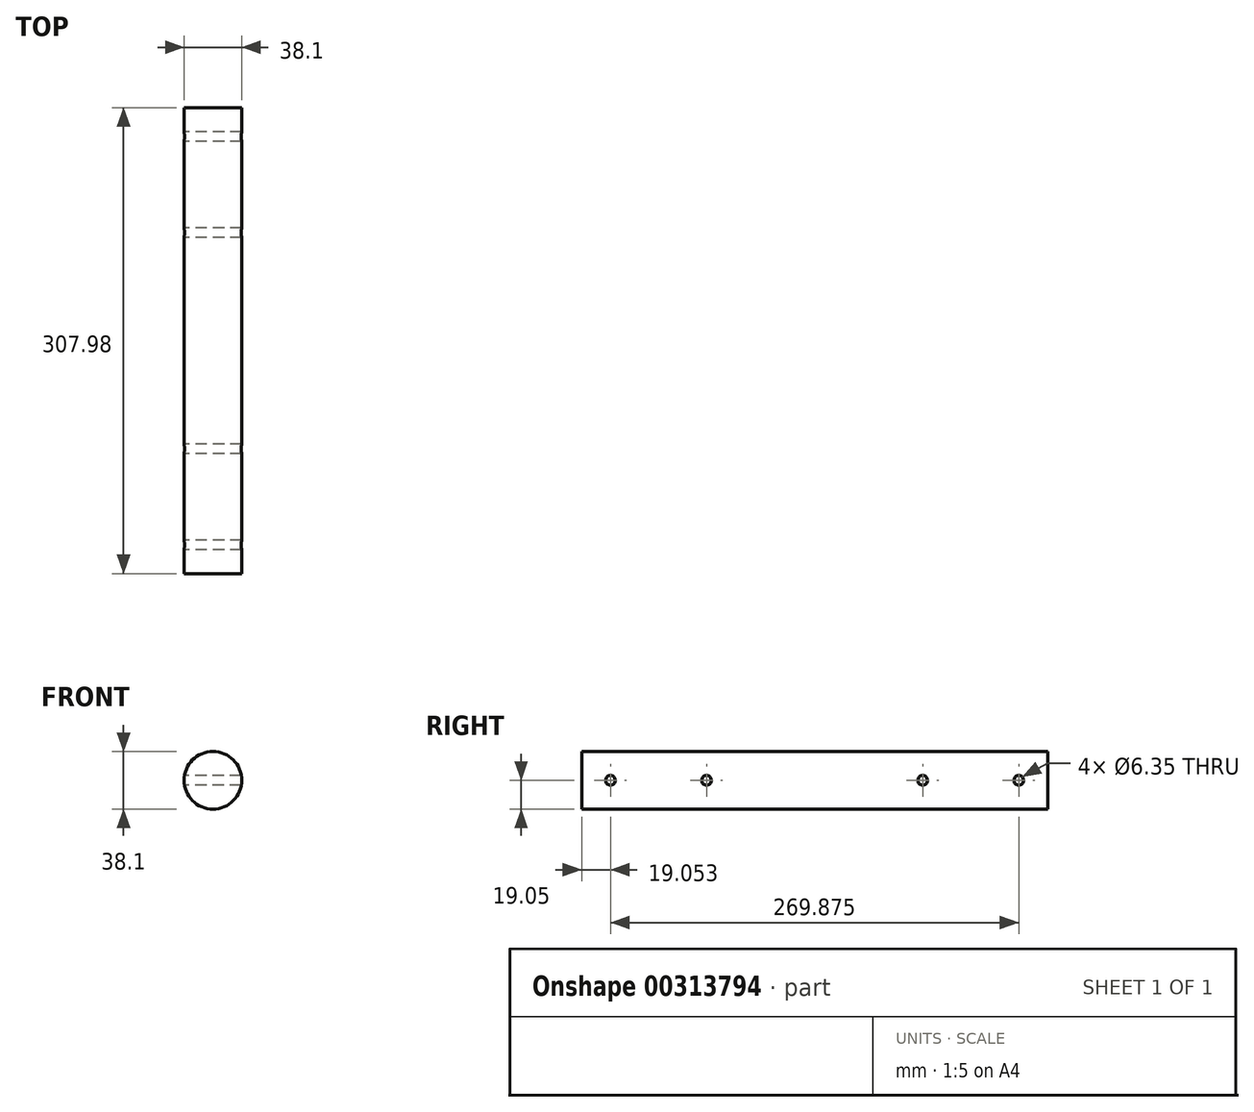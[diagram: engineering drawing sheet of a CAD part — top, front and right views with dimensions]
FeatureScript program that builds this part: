
annotation { "Feature Type Name" : "Feature", "Feature Type Description" : "" }
export const myFeature = defineFeature(function(context is Context, id is Id, definition is map)
    precondition{}
    {
        {
            var Q0;
            Q0=qCreatedBy(makeId("Front.planeOp"),FACE);
            var sketch = newSketch(context, id + "F0", { "sketchPlane" : qUnion([Q0])});
            skCircle(sketch, "E0", {"center": v(0, 0) * mm, "radius": 19.05 * mm});
            skSolve(sketch);
        }
        {
            var Q0;
            Q0 = qSketchRegion(id + "F0", true);
            extrude(context, id + "F1", {"entities" : qUnion([Q0]), "endBound" : BoundingType.SYMMETRIC, "depth" : 307.97 * mm});
        }
        {
            var Q0;
            Q0=qCreatedBy(makeId("Right.planeOp"),FACE);
            var sketch = newSketch(context, id + "F2", { "sketchPlane" : qUnion([Q0])});
            skCircle(sketch, "E1", {"center": v(-134.94, 0) * mm, "radius": 3.18 * mm});
            skCircle(sketch, "E2", {"center": v(134.94, 0) * mm, "radius": 3.18 * mm});
            skCircle(sketch, "E3", {"center": v(-71.44, 0) * mm, "radius": 3.18 * mm});
            skCircle(sketch, "E4", {"center": v(71.44, 0) * mm, "radius": 3.17 * mm});
            skSolve(sketch);
        }
        {
            var Q0;
            Q0 = qSketchRegion(id + "F2", true);
            extrude(context, id + "F3", {"entities" : qUnion([Q0]), "operationType" : NewBodyOperationType.REMOVE, "endBound" : BoundingType.THROUGH_ALL, "depth" : 25.4 * mm, "hasSecondDirection" : true, "secondDirectionBound" : SecondDirectionBoundingType.THROUGH_ALL, "secondDirectionOppositeDirection" : true, "secondDirectionDepth" : 25.4 * mm});
        }
    });
